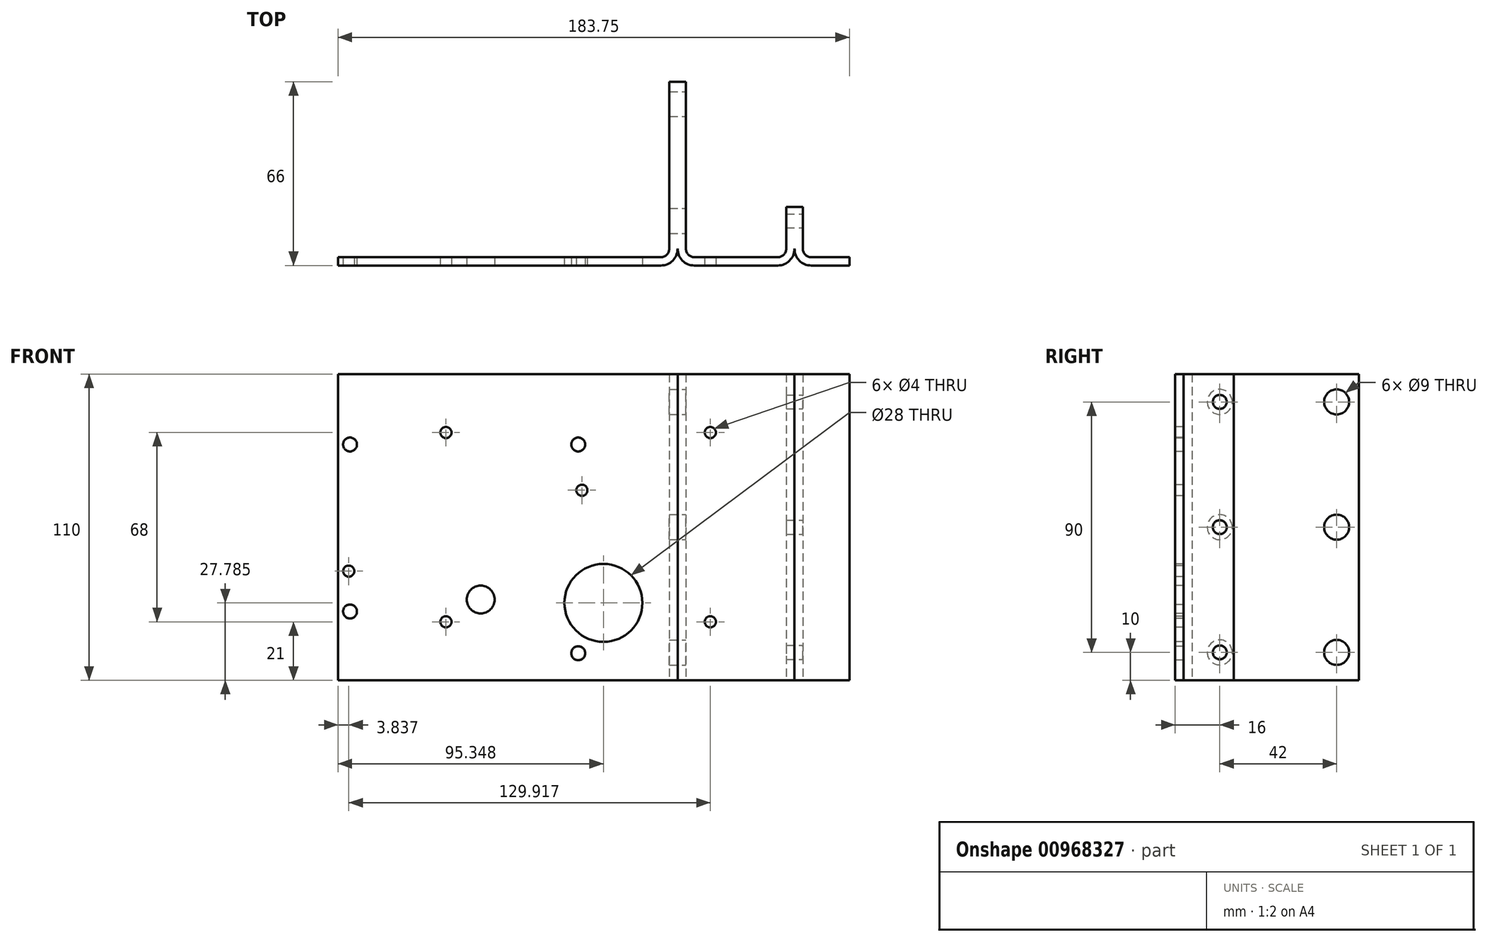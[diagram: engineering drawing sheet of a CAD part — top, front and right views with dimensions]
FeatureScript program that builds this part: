
annotation { "Feature Type Name" : "Feature", "Feature Type Description" : "" }
export const myFeature = defineFeature(function(context is Context, id is Id, definition is map)
    precondition{}
    {
        {
            var Q0;
            Q0=qCreatedBy(makeId("Top.planeOp"),FACE);
            var sketch = newSketch(context, id + "F0", { "sketchPlane" : qUnion([Q0])});
            skLineSegment(sketch, "E0", {"start": v(-42, 45) * mm, "end": v(-42, -15) * mm});
            skLineSegment(sketch, "E1", {"start": v(-42, 45) * mm, "end": v(-39, 45) * mm});
            skLineSegment(sketch, "E2", {"start": v(-39, 45) * mm, "end": v(-39, -15) * mm});
            skLineSegment(sketch, "E3", {"start": v(-3, -15) * mm, "end": v(-3, 0) * mm});
            skLineSegment(sketch, "E4", {"start": v(-3, 0) * mm, "end": v(3, 0) * mm});
            skLineSegment(sketch, "E5", {"start": v(3, 0) * mm, "end": v(3, -15) * mm});
            skLineSegment(sketch, "E6", {"start": v(-36, -18) * mm, "end": v(-6, -18) * mm});
            skLineSegment(sketch, "E7", {"start": v(-36, -21) * mm, "end": v(-6, -21) * mm});
            skLineSegment(sketch, "E8", {"start": v(6, -18) * mm, "end": v(19.75, -18) * mm});
            skLineSegment(sketch, "E9", {"start": v(6, -21) * mm, "end": v(19.75, -21) * mm});
            skLineSegment(sketch, "E10", {"start": v(19.75, -21) * mm, "end": v(19.75, -18) * mm});
            skArc(sketch, "E11", {"start": v(-39, -15) * mm, "mid": v(-38.12, -17.12) * mm, "end": v(-36, -18) * mm});
            skArc(sketch, "E12", {"start": v(-42, -15) * mm, "mid": v(-40.24, -19.24) * mm, "end": v(-36, -21) * mm});
            skArc(sketch, "E13", {"start": v(-6, -18) * mm, "mid": v(-3.88, -17.12) * mm, "end": v(-3, -15) * mm});
            skPoint(sketch, "E14", {"position": v(0, -15) * mm});
            skArc(sketch, "E15", {"start": v(-6, -21) * mm, "mid": v(-1.76, -19.24) * mm, "end": v(0, -15) * mm});
            skArc(sketch, "E16", {"start": v(3, -15) * mm, "mid": v(3.88, -17.12) * mm, "end": v(6, -18) * mm});
            skArc(sketch, "E17", {"start": v(0, -15) * mm, "mid": v(1.76, -19.24) * mm, "end": v(6, -21) * mm});
            skSolve(sketch);
        }
        {
            var Q0;
            Q0 = qSketchRegion(id + "F0", true);
            extrude(context, id + "F1", {"entities" : qUnion([Q0]), "depth" : 55 * mm, "offsetDistance" : 25 * mm, "hasSecondDirection" : true, "secondDirectionOppositeDirection" : true, "secondDirectionDepth" : 55 * mm});
        }
        {
            var Q0;
            Q0=makeQuery(id+"F1.opExtrude","SWEPT_FACE",FACE,{"disambiguationData":[OSD([sQuery(id+"F0.wireOp",EDGE,"E5")])]});
            var sketch = newSketch(context, id + "F2", { "sketchPlane" : qUnion([Q0])});
            skCircle(sketch, "E18", {"center": v(-5, 45) * mm, "radius": 2.5 * mm});
            skCircle(sketch, "E19", {"center": v(-5, 0) * mm, "radius": 2.5 * mm});
            skCircle(sketch, "E20", {"center": v(-5, -45) * mm, "radius": 2.5 * mm});
            skSolve(sketch);
        }
        {
            var Q0;
            Q0 = qSketchRegion(id + "F2", true);
            var Q1;
            Q1=makeQuery(id+"F1.opExtrude","SWEPT_BODY",BODY,{"disambiguationData":[OSD([sQuery(id+"F0.wireOp",EDGE,"E0"),sQuery(id+"F0.wireOp",EDGE,"E1"),sQuery(id+"F0.wireOp",EDGE,"E2"),sQuery(id+"F0.wireOp",EDGE,"E3"),sQuery(id+"F0.wireOp",EDGE,"E4"),sQuery(id+"F0.wireOp",EDGE,"E5"),sQuery(id+"F0.wireOp",EDGE,"E6"),sQuery(id+"F0.wireOp",EDGE,"E7"),sQuery(id+"F0.wireOp",EDGE,"E8"),sQuery(id+"F0.wireOp",EDGE,"E9"),sQuery(id+"F0.wireOp",EDGE,"E10"),sQuery(id+"F0.wireOp",EDGE,"E11"),sQuery(id+"F0.wireOp",EDGE,"E12"),sQuery(id+"F0.wireOp",EDGE,"E13"),sQuery(id+"F0.wireOp",EDGE,"E15"),sQuery(id+"F0.wireOp",EDGE,"E16"),sQuery(id+"F0.wireOp",EDGE,"E17")])]});
            extrude(context, id + "F3", {"entities" : qUnion([Q0]), "operationType" : NewBodyOperationType.REMOVE, "endBound" : BoundingType.THROUGH_ALL, "oppositeDirection" : true, "depth" : 25 * mm, "endBoundEntityBody" : qUnion([Q1]), "offsetDistance" : 25 * mm});
        }
        {
            var Q0;
            Q0=qCreatedBy(makeId("Top.planeOp"),FACE);
            var sketch = newSketch(context, id + "F4", { "sketchPlane" : qUnion([Q0])});
            skLineSegment(sketch, "E21", {"start": v(-42, 45) * mm, "end": v(-42, -15) * mm});
            skLineSegment(sketch, "E22", {"start": v(-42, 45) * mm, "end": v(-45, 45) * mm});
            skLineSegment(sketch, "E23", {"start": v(-45, 45) * mm, "end": v(-45, -15) * mm});
            skLineSegment(sketch, "E24", {"start": v(-48, -21) * mm, "end": v(-164, -21) * mm});
            skLineSegment(sketch, "E25", {"start": v(-164, -21) * mm, "end": v(-164, -18) * mm});
            skArc(sketch, "E26", {"start": v(-48, -18) * mm, "mid": v(-45.88, -17.12) * mm, "end": v(-45, -15) * mm});
            skArc(sketch, "E27", {"start": v(-48, -21) * mm, "mid": v(-43.76, -19.24) * mm, "end": v(-42, -15) * mm});
            skLineSegment(sketch, "E28", {"start": v(-164, -18) * mm, "end": v(-48, -18) * mm});
            skSolve(sketch);
        }
        {
            var Q0;
            Q0 = qSketchRegion(id + "F4", true);
            extrude(context, id + "F5", {"entities" : qUnion([Q0]), "operationType" : NewBodyOperationType.ADD, "depth" : 55 * mm, "offsetDistance" : 25 * mm, "hasSecondDirection" : true, "secondDirectionOppositeDirection" : true, "secondDirectionDepth" : 55 * mm});
        }
        {
            var Q0;
            Q0=makeQuery(id+"F1.opExtrude","SWEPT_FACE",FACE,{"disambiguationData":[OSD([sQuery(id+"F0.wireOp",EDGE,"E2")])]});
            var sketch = newSketch(context, id + "F6", { "sketchPlane" : qUnion([Q0])});
            skCircle(sketch, "E29", {"center": v(-5, 45) * mm, "radius": 4.5 * mm});
            skCircle(sketch, "E30", {"center": v(-5, 0) * mm, "radius": 4.5 * mm});
            skCircle(sketch, "E31", {"center": v(-5, -45) * mm, "radius": 4.5 * mm});
            skSolve(sketch);
        }
        {
            var Q0;
            Q0 = qSketchRegion(id + "F6", true);
            extrude(context, id + "F7", {"entities" : qUnion([Q0]), "operationType" : NewBodyOperationType.REMOVE, "oppositeDirection" : true, "depth" : 6 * mm, "offsetDistance" : 25 * mm});
        }
        {
            var Q0;
            Q0=makeQuery(id+"F1.opExtrude","SWEPT_FACE",FACE,{"disambiguationData":[OSD([sQuery(id+"F0.wireOp",EDGE,"E2")])]});
            var sketch = newSketch(context, id + "F8", { "sketchPlane" : qUnion([Q0])});
            skCircle(sketch, "E32", {"center": v(37, 0) * mm, "radius": 4.5 * mm});
            skCircle(sketch, "E33", {"center": v(37, -45) * mm, "radius": 4.5 * mm});
            skCircle(sketch, "E34", {"center": v(37, 45) * mm, "radius": 4.5 * mm});
            skSolve(sketch);
        }
        {
            var Q0;
            Q0 = qSketchRegion(id + "F8", true);
            extrude(context, id + "F9", {"entities" : qUnion([Q0]), "operationType" : NewBodyOperationType.REMOVE, "oppositeDirection" : true, "depth" : 6 * mm, "offsetDistance" : 25 * mm});
        }
        {
            var Q0;
            Q0=makeQuery(id+"F5.opExtrude","SWEPT_FACE",FACE,{"disambiguationData":[OSD([sQuery(id+"F4.wireOp",EDGE,"E24")])]});
            var sketch = newSketch(context, id + "F10", { "sketchPlane" : qUnion([Q0])});
            skCircle(sketch, "E35", {"center": v(-30.25, -34) * mm, "radius": 2 * mm});
            skCircle(sketch, "E36", {"center": v(-30.25, 34) * mm, "radius": 2 * mm});
            skCircle(sketch, "E37", {"center": v(-125.25, 34) * mm, "radius": 2 * mm});
            skCircle(sketch, "E38", {"center": v(-125.25, -34) * mm, "radius": 2 * mm});
            skSolve(sketch);
        }
        {
            var Q0;
            Q0 = qSketchRegion(id + "F10", true);
            extrude(context, id + "F11", {"entities" : qUnion([Q0]), "operationType" : NewBodyOperationType.REMOVE, "oppositeDirection" : true, "depth" : 3 * mm, "offsetDistance" : 25 * mm});
        }
        {
            var Q0;
            Q0=makeQuery(id+"F5.opExtrude","SWEPT_FACE",FACE,{"disambiguationData":[OSD([sQuery(id+"F4.wireOp",EDGE,"E24")])]});
            var sketch = newSketch(context, id + "F12", { "sketchPlane" : qUnion([Q0])});
            skCircle(sketch, "E39", {"center": v(-68.65, -27.22) * mm, "radius": 14 * mm});
            skSolve(sketch);
        }
        {
            var Q0;
            Q0 = qSketchRegion(id + "F12", true);
            extrude(context, id + "F13", {"entities" : qUnion([Q0]), "operationType" : NewBodyOperationType.REMOVE, "oppositeDirection" : true, "depth" : 3 * mm, "offsetDistance" : 25 * mm});
        }
        {
            var Q0;
            Q0=makeQuery(id+"F5.opExtrude","SWEPT_FACE",FACE,{"disambiguationData":[OSD([sQuery(id+"F4.wireOp",EDGE,"E24")])]});
            var sketch = newSketch(context, id + "F14", { "sketchPlane" : qUnion([Q0])});
            skCircle(sketch, "E40", {"center": v(-159.7, 29.7) * mm, "radius": 2.5 * mm});
            skCircle(sketch, "E41", {"center": v(-159.7, -30.3) * mm, "radius": 2.5 * mm});
            skCircle(sketch, "E42", {"center": v(-77.7, 29.7) * mm, "radius": 2.5 * mm});
            skCircle(sketch, "E43", {"center": v(-77.7, -45.3) * mm, "radius": 2.5 * mm});
            skSolve(sketch);
        }
        {
            var Q0;
            Q0 = qSketchRegion(id + "F14", true);
            extrude(context, id + "F15", {"entities" : qUnion([Q0]), "operationType" : NewBodyOperationType.REMOVE, "oppositeDirection" : true, "depth" : 3 * mm, "offsetDistance" : 25 * mm});
        }
        {
            var Q0;
            Q0=makeQuery(id+"F5.opExtrude","SWEPT_FACE",FACE,{"disambiguationData":[OSD([sQuery(id+"F4.wireOp",EDGE,"E24")])]});
            var sketch = newSketch(context, id + "F16", { "sketchPlane" : qUnion([Q0])});
            skCircle(sketch, "E44", {"center": v(-112.75, -26) * mm, "radius": 5 * mm});
            skSolve(sketch);
        }
        {
            var Q0;
            Q0 = qSketchRegion(id + "F16", true);
            extrude(context, id + "F17", {"entities" : qUnion([Q0]), "operationType" : NewBodyOperationType.REMOVE, "oppositeDirection" : true, "depth" : 3 * mm, "offsetDistance" : 25 * mm});
        }
        {
            var Q0;
            Q0=makeQuery(id+"F5.opExtrude","SWEPT_FACE",FACE,{"disambiguationData":[OSD([sQuery(id+"F4.wireOp",EDGE,"E24")])]});
            var sketch = newSketch(context, id + "F18", { "sketchPlane" : qUnion([Q0])});
            skCircle(sketch, "E45", {"center": v(-76.4, 13.25) * mm, "radius": 2 * mm});
            skCircle(sketch, "E46", {"center": v(-160.16, -15.8) * mm, "radius": 2 * mm});
            skSolve(sketch);
        }
        {
            var Q0;
            Q0 = qSketchRegion(id + "F18", true);
            extrude(context, id + "F19", {"entities" : qUnion([Q0]), "operationType" : NewBodyOperationType.REMOVE, "oppositeDirection" : true, "depth" : 3 * mm, "offsetDistance" : 25 * mm});
        }
    });
